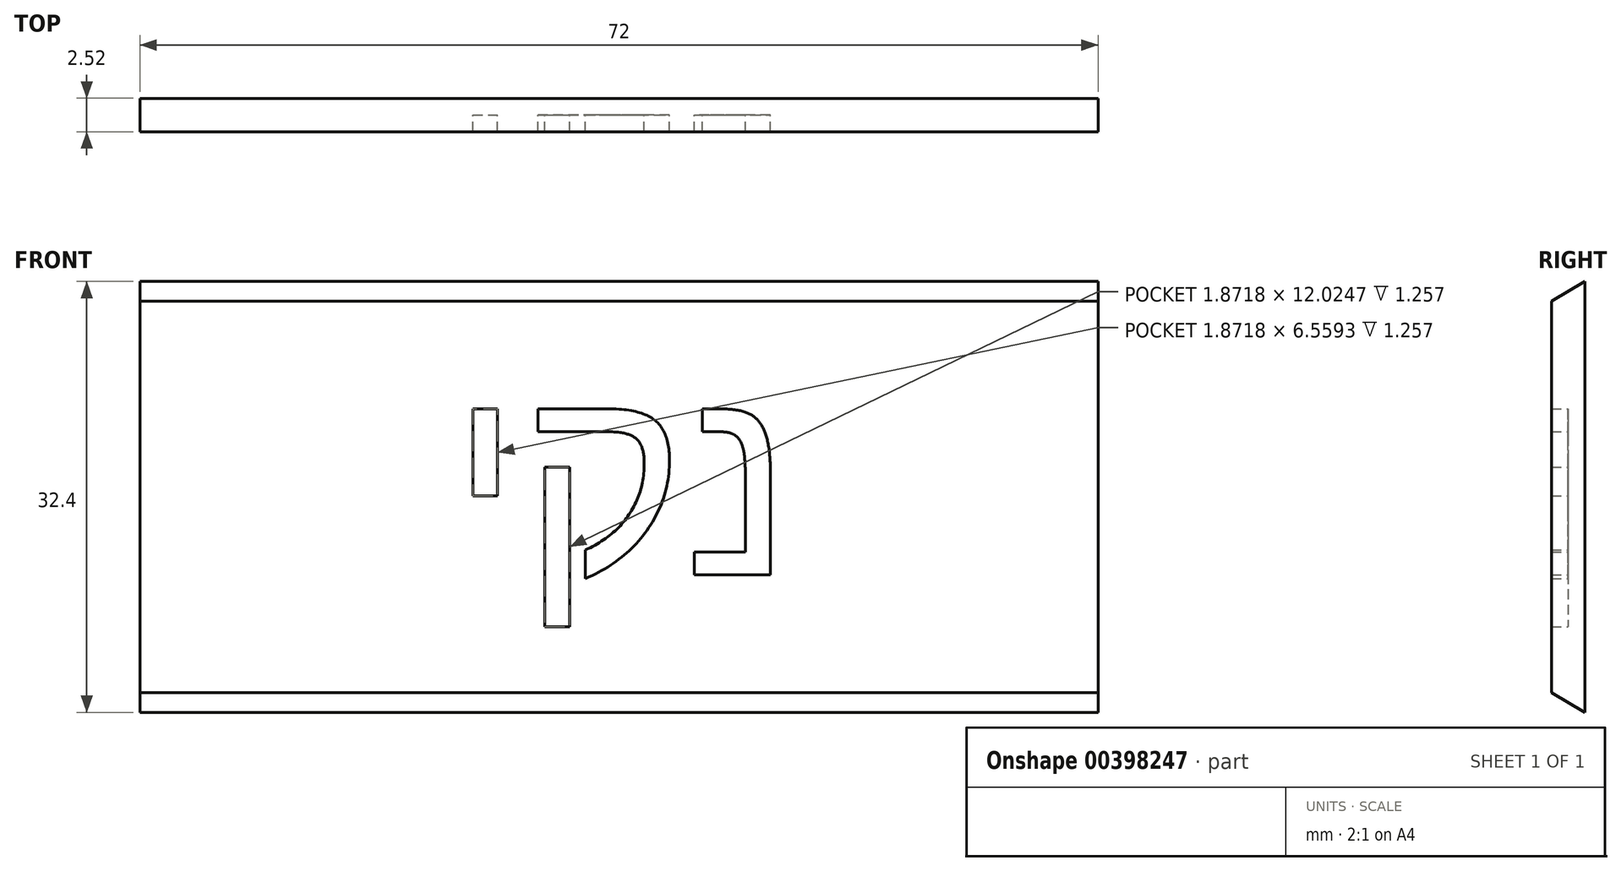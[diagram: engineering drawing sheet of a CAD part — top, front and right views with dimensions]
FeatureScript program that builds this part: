
annotation { "Feature Type Name" : "Feature", "Feature Type Description" : "" }
export const myFeature = defineFeature(function(context is Context, id is Id, definition is map)
    precondition{}
    {
        {
            var Q0;
            Q0=qCreatedBy(makeId("Right.planeOp"),FACE);
            var sketch = newSketch(context, id + "F0", { "sketchPlane" : qUnion([Q0])});
            skLineSegment(sketch, "E0", {"start": v(1.26, 16.2) * mm, "end": v(-1.26, 14.72) * mm});
            skLineSegment(sketch, "E1", {"start": v(-1.26, 14.72) * mm, "end": v(-1.26, -14.72) * mm});
            skLineSegment(sketch, "E2", {"start": v(-1.26, -14.72) * mm, "end": v(1.26, -16.2) * mm});
            skLineSegment(sketch, "E3", {"start": v(1.26, -16.2) * mm, "end": v(1.26, 16.2) * mm});
            skSolve(sketch);
        }
        {
            var Q0;
            Q0 = qSketchRegion(id + "F0", true);
            extrude(context, id + "F1", {"entities" : qUnion([Q0]), "endBound" : BoundingType.SYMMETRIC, "depth" : 72 * mm});
        }
        {
            var Q0;
            Q0=qCreatedBy(makeId("Front.planeOp"),FACE);
            var sketch = newSketch(context, id + "F2", { "sketchPlane" : qUnion([Q0])});
            skText(sketch, "E4", { "text": "יקנ", "fontName": "Arimo-Regular.ttf"});
            const initialGuessF2  = {"E4": [-0.01277, -0.00586, 1, 0, 0.015]};
            skSetInitialGuess(sketch, initialGuessF2);
            skSolve(sketch);
        }
        {
            var Q0;
            Q0 = qSketchRegion(id + "F2", true);
            extrude(context, id + "F3", {"entities" : qUnion([Q0]), "operationType" : NewBodyOperationType.REMOVE, "depth" : 1.3 * mm});
        }
    });
